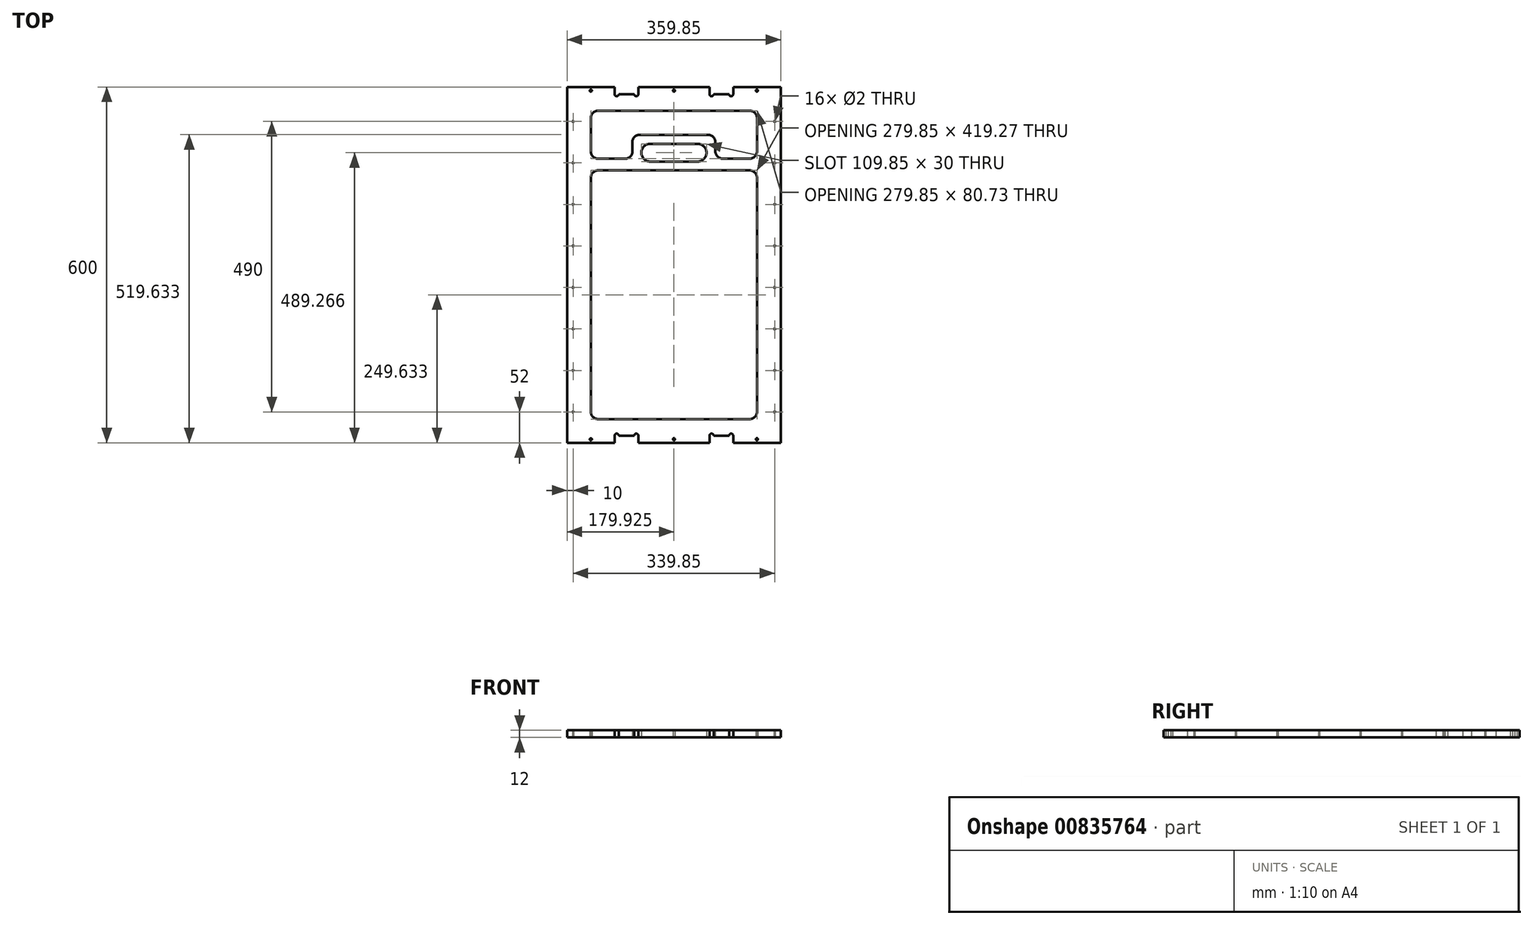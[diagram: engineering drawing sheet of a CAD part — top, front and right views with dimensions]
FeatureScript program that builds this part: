
annotation { "Feature Type Name" : "Feature", "Feature Type Description" : "" }
export const myFeature = defineFeature(function(context is Context, id is Id, definition is map)
    precondition{}
    {
        {
            var Q0;
            Q0=qCreatedBy(makeId("Top.planeOp"),FACE);
            var sketch = newSketch(context, id + "F0", { "sketchPlane" : qUnion([Q0])});
            skLineSegment(sketch, "E0.bottom", {"start": v(0, 0) * mm, "end": v(359.85, 0) * mm});
            skLineSegment(sketch, "E0.top", {"start": v(0, 600) * mm, "end": v(359.85, 600) * mm});
            skLineSegment(sketch, "E0.left", {"start": v(0, 0) * mm, "end": v(0, 600) * mm});
            skLineSegment(sketch, "E0.right", {"start": v(359.85, 0) * mm, "end": v(359.85, 600) * mm});
            skLineSegment(sketch, "E1", {"start": v(40, 600) * mm, "end": v(40, 0) * mm, "construction": true});
            skLineSegment(sketch, "E2", {"start": v(319.85, 0) * mm, "end": v(319.85, 600) * mm, "construction": true});
            skLineSegment(sketch, "E3", {"start": v(359.85, 560) * mm, "end": v(0, 560) * mm, "construction": true});
            skLineSegment(sketch, "E4", {"start": v(0, 40) * mm, "end": v(359.85, 40) * mm, "construction": true});
            skLineSegment(sketch, "E5", {"start": v(359.85, 479.27) * mm, "end": v(0, 479.27) * mm, "construction": true});
            skLineSegment(sketch, "E6", {"start": v(0, 459.27) * mm, "end": v(359.85, 459.27) * mm, "construction": true});
            skLineSegment(sketch, "E7", {"start": v(52, 560) * mm, "end": v(307.85, 560) * mm});
            skLineSegment(sketch, "E8", {"start": v(319.85, 548) * mm, "end": v(319.85, 491.27) * mm});
            skLineSegment(sketch, "E9", {"start": v(307.85, 479.27) * mm, "end": v(261.85, 479.27) * mm});
            skLineSegment(sketch, "E10", {"start": v(249.85, 491.27) * mm, "end": v(249.85, 507.27) * mm});
            skLineSegment(sketch, "E11", {"start": v(237.85, 519.27) * mm, "end": v(122, 519.27) * mm});
            skLineSegment(sketch, "E12", {"start": v(110, 507.27) * mm, "end": v(110, 491.27) * mm});
            skLineSegment(sketch, "E13", {"start": v(98, 479.27) * mm, "end": v(52, 479.27) * mm});
            skLineSegment(sketch, "E14", {"start": v(40, 491.27) * mm, "end": v(40, 548) * mm});
            skLineSegment(sketch, "E15", {"start": v(52, 459.27) * mm, "end": v(307.85, 459.27) * mm});
            skLineSegment(sketch, "E16", {"start": v(319.85, 447.27) * mm, "end": v(319.85, 52) * mm});
            skLineSegment(sketch, "E17", {"start": v(307.85, 40) * mm, "end": v(52, 40) * mm});
            skLineSegment(sketch, "E18", {"start": v(40, 52) * mm, "end": v(40, 447.27) * mm});
            skPoint(sketch, "E19.visualSharp", {"position": v(40, 459.27) * mm});
            skArc(sketch, "E19.filletArc", {"start": v(52, 459.27) * mm, "mid": v(43.51, 455.75) * mm, "end": v(40, 447.27) * mm});
            skPoint(sketch, "E20.visualSharp", {"position": v(319.85, 459.27) * mm});
            skArc(sketch, "E20.filletArc", {"start": v(319.85, 447.27) * mm, "mid": v(316.34, 455.75) * mm, "end": v(307.85, 459.27) * mm});
            skPoint(sketch, "E21.visualSharp", {"position": v(319.85, 479.27) * mm});
            skArc(sketch, "E21.filletArc", {"start": v(307.85, 479.27) * mm, "mid": v(316.34, 482.78) * mm, "end": v(319.85, 491.27) * mm});
            skPoint(sketch, "E22.visualSharp", {"position": v(249.85, 479.27) * mm});
            skArc(sketch, "E22.filletArc", {"start": v(249.85, 491.27) * mm, "mid": v(253.36, 482.78) * mm, "end": v(261.85, 479.27) * mm});
            skPoint(sketch, "E23.visualSharp", {"position": v(249.85, 519.27) * mm});
            skArc(sketch, "E23.filletArc", {"start": v(249.85, 507.27) * mm, "mid": v(246.34, 515.75) * mm, "end": v(237.85, 519.27) * mm});
            skPoint(sketch, "E24.visualSharp", {"position": v(110, 519.27) * mm});
            skArc(sketch, "E24.filletArc", {"start": v(122, 519.27) * mm, "mid": v(113.51, 515.75) * mm, "end": v(110, 507.27) * mm});
            skPoint(sketch, "E25.visualSharp", {"position": v(110, 479.27) * mm});
            skArc(sketch, "E25.filletArc", {"start": v(98, 479.27) * mm, "mid": v(106.49, 482.78) * mm, "end": v(110, 491.27) * mm});
            skPoint(sketch, "E26.visualSharp", {"position": v(40, 479.27) * mm});
            skArc(sketch, "E26.filletArc", {"start": v(40, 491.27) * mm, "mid": v(43.51, 482.78) * mm, "end": v(52, 479.27) * mm});
            skPoint(sketch, "E27.visualSharp", {"position": v(40, 560) * mm});
            skArc(sketch, "E27.filletArc", {"start": v(52, 560) * mm, "mid": v(43.51, 556.49) * mm, "end": v(40, 548) * mm});
            skPoint(sketch, "E28.visualSharp", {"position": v(319.85, 560) * mm});
            skArc(sketch, "E28.filletArc", {"start": v(319.85, 548) * mm, "mid": v(316.34, 556.49) * mm, "end": v(307.85, 560) * mm});
            skPoint(sketch, "E29.visualSharp", {"position": v(319.85, 40) * mm});
            skArc(sketch, "E29.filletArc", {"start": v(307.85, 40) * mm, "mid": v(316.34, 43.51) * mm, "end": v(319.85, 52) * mm});
            skPoint(sketch, "E30.visualSharp", {"position": v(40, 40) * mm});
            skArc(sketch, "E30.filletArc", {"start": v(40, 52) * mm, "mid": v(43.51, 43.51) * mm, "end": v(52, 40) * mm});
            skLineSegment(sketch, "E31", {"start": v(140, 489.27) * mm, "end": v(219.85, 489.27) * mm});
            skArc(sketch, "E32.0.startCap", {"start": v(140, 474.27) * mm, "mid": v(125, 489.27) * mm, "end": v(140, 504.27) * mm});
            skArc(sketch, "E32.0.endCap", {"start": v(219.85, 504.27) * mm, "mid": v(234.85, 489.27) * mm, "end": v(219.85, 474.27) * mm});
            skLineSegment(sketch, "E32.0.left", {"start": v(140, 504.27) * mm, "end": v(219.85, 504.27) * mm});
            skLineSegment(sketch, "E32.0.right", {"start": v(140, 474.27) * mm, "end": v(219.85, 474.27) * mm});
            skCircle(sketch, "E33", {"center": v(10, 52) * mm, "radius": 1 * mm});
            skLineSegment(sketch, "E34", {"start": v(-24.67, 52) * mm, "end": v(376.85, 52) * mm, "construction": true});
            skCircle(sketch, "E35", {"center": v(349.85, 52) * mm, "radius": 1 * mm});
            skCircle(sketch, "E36.0.1.0", {"center": v(10, 122) * mm, "radius": 1 * mm});
            skCircle(sketch, "E36.0.1.1", {"center": v(349.85, 122) * mm, "radius": 1 * mm});
            skCircle(sketch, "E36.0.2.0", {"center": v(10, 192) * mm, "radius": 1 * mm});
            skCircle(sketch, "E36.0.2.1", {"center": v(349.85, 192) * mm, "radius": 1 * mm});
            skCircle(sketch, "E36.0.3.0", {"center": v(10, 262) * mm, "radius": 1 * mm});
            skCircle(sketch, "E36.0.3.1", {"center": v(349.85, 262) * mm, "radius": 1 * mm});
            skCircle(sketch, "E36.0.4.0", {"center": v(10, 332) * mm, "radius": 1 * mm});
            skCircle(sketch, "E36.0.4.1", {"center": v(349.85, 332) * mm, "radius": 1 * mm});
            skCircle(sketch, "E36.0.5.0", {"center": v(10, 402) * mm, "radius": 1 * mm});
            skCircle(sketch, "E36.0.5.1", {"center": v(349.85, 402) * mm, "radius": 1 * mm});
            skCircle(sketch, "E36.0.6.0", {"center": v(10, 472) * mm, "radius": 1 * mm});
            skCircle(sketch, "E36.0.6.1", {"center": v(349.85, 472) * mm, "radius": 1 * mm});
            skLineSegment(sketch, "E36.direction1", {"start": v(10, 52) * mm, "end": v(35, 52) * mm, "construction": true});
            skLineSegment(sketch, "E36.direction2", {"start": v(10, 52) * mm, "end": v(10, 122) * mm, "construction": true});
            skCircle(sketch, "E37.0.0.7", {"center": v(10, 542) * mm, "radius": 1 * mm});
            skCircle(sketch, "E37.2.0.7", {"center": v(349.85, 542) * mm, "radius": 1 * mm});
            skLineSegment(sketch, "E38", {"start": v(80, 0) * mm, "end": v(80, 12) * mm});
            skLineSegment(sketch, "E39", {"start": v(120, 12) * mm, "end": v(120, 0) * mm});
            skLineSegment(sketch, "E40", {"start": v(239.85, 0) * mm, "end": v(239.85, 12) * mm});
            skLineSegment(sketch, "E41", {"start": v(279.85, 12) * mm, "end": v(279.85, 0) * mm});
            skLineSegment(sketch, "E42", {"start": v(80, 600) * mm, "end": v(80, 588) * mm});
            skLineSegment(sketch, "E43", {"start": v(120, 588) * mm, "end": v(120, 600) * mm});
            skLineSegment(sketch, "E44", {"start": v(239.85, 600) * mm, "end": v(239.85, 588) * mm});
            skLineSegment(sketch, "E45", {"start": v(246.85, 588) * mm, "end": v(272.85, 588) * mm});
            skLineSegment(sketch, "E46", {"start": v(279.85, 588) * mm, "end": v(279.85, 600) * mm});
            skLineSegment(sketch, "E47", {"start": v(0, 6) * mm, "end": v(359.85, 6) * mm, "construction": true});
            skCircle(sketch, "E48", {"center": v(179.93, 6) * mm, "radius": 1.75 * mm});
            skCircle(sketch, "E49", {"center": v(319.85, 6) * mm, "radius": 1.75 * mm});
            skCircle(sketch, "E50", {"center": v(40, 6) * mm, "radius": 1.75 * mm});
            skLineSegment(sketch, "E51", {"start": v(0, 594) * mm, "end": v(359.85, 594) * mm, "construction": true});
            skCircle(sketch, "E52", {"center": v(179.93, 594) * mm, "radius": 1.75 * mm});
            skCircle(sketch, "E53", {"center": v(319.85, 594) * mm, "radius": 1.75 * mm});
            skCircle(sketch, "E54", {"center": v(40, 594) * mm, "radius": 1.75 * mm});
            skArc(sketch, "E55", {"start": v(80, 12) * mm, "mid": v(83.5, 15.5) * mm, "end": v(87, 12) * mm});
            skArc(sketch, "E56", {"start": v(120, 12) * mm, "mid": v(116.5, 15.5) * mm, "end": v(113, 12) * mm});
            skArc(sketch, "E57", {"start": v(239.85, 12) * mm, "mid": v(243.35, 15.5) * mm, "end": v(246.85, 12) * mm});
            skArc(sketch, "E58", {"start": v(279.85, 12) * mm, "mid": v(276.35, 15.5) * mm, "end": v(272.85, 12) * mm});
            skLineSegment(sketch, "E59.trimOffspring", {"start": v(246.85, 12) * mm, "end": v(272.85, 12) * mm});
            skLineSegment(sketch, "E60.trimOffspring", {"start": v(87, 12) * mm, "end": v(113, 12) * mm});
            skArc(sketch, "E61", {"start": v(80, 588) * mm, "mid": v(83.5, 584.5) * mm, "end": v(87, 588) * mm});
            skArc(sketch, "E62", {"start": v(120, 588) * mm, "mid": v(116.5, 584.5) * mm, "end": v(113, 588) * mm});
            skArc(sketch, "E63", {"start": v(239.85, 588) * mm, "mid": v(243.35, 584.5) * mm, "end": v(246.85, 588) * mm});
            skArc(sketch, "E64", {"start": v(279.85, 588) * mm, "mid": v(276.35, 584.5) * mm, "end": v(272.85, 588) * mm});
            skLineSegment(sketch, "E65.trimOffspring", {"start": v(87, 588) * mm, "end": v(113, 588) * mm});
            skSolve(sketch);
        }
        {
            var Q0;
            Q0=makeQuery(id+"F0.imprint","IMPRINT",FACE,{"disambiguationData":[TD([[makeQuery(id+"F0.imprint","IMPRINT",EDGE,{"derivedFrom":sQuery(id+"F0.wireOp",EDGE,"E0.bottom")}),1.0]])]});
            extrude(context, id + "F1", {"entities" : qUnion([Q0]), "depth" : 12 * mm, "offsetDistance" : 25 * mm});
        }
    });
